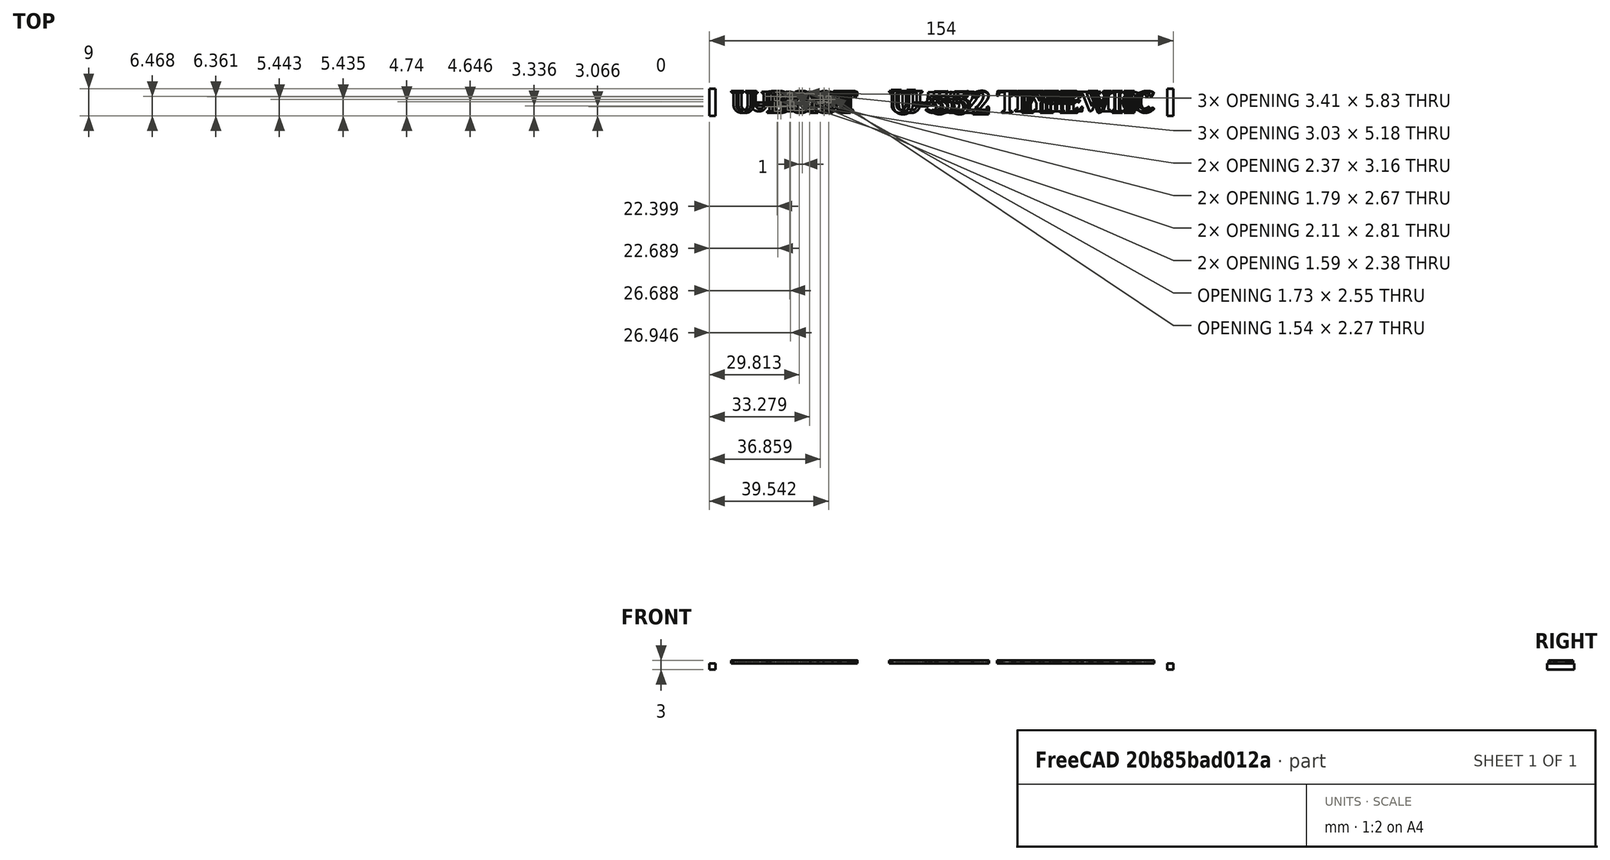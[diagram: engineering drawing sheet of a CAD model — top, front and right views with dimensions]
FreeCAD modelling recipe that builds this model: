
FCSTD DOCUMENT  (FreeCAD 0.18R16146 (Git))
Label: U-Boat Stand Nameplate
License: All rights reserved
LicenseURL: http://en.wikipedia.org/wiki/All_rights_reserved
objects: Part::FeaturePython×44, Part::Feature×12, Part::Part2DObjectPython×7, Part::Extrusion×7, App::DocumentObjectGroup×4, Sketcher::SketchObject×2, Part::Face×2, Part::Box×2, Mesh::Feature×1, Part::Compound×1
note: 77 computed .brp shape members not serialized (recipe doc carries the construction recipe); baked Part::Feature solids carry a one-line shape summary decoded from their .brp

FEATURE [Mesh::Feature] U_Boot_Stand_2  label="U-Boot-Stand-2"
FEATURE [Part::Feature] U_Boot_Stand_2001
  shape: bbox 154 x 20 x 3 mm, 3614 faces, 0 solids (baked)
FEATURE [Part::Feature] U_Boot_Stand_2001001  label="U_Boot_Stand_2002"
  shape: bbox 154 x 20 x 3 mm, 1660 faces, 0 solids (baked)
FEATURE [Sketcher::SketchObject] Sketch
  sketch-geometry (4):
    g0: LineSegment StartX=143.756 StartY=1.09319 StartZ=0 EndX=12.9474 EndY=1.09319 EndZ=0
    g1: LineSegment StartX=12.9474 StartY=1.09319 StartZ=0 EndX=12.9474 EndY=11.5235 EndZ=0
    g2: LineSegment StartX=12.9474 StartY=11.5235 StartZ=0 EndX=143.756 EndY=11.5235 EndZ=0
    g3: LineSegment StartX=143.756 StartY=11.5235 StartZ=0 EndX=143.756 EndY=1.09319 EndZ=0
  constraints (8):
    c: Coincident(g0,g1)
    c: Coincident(g1,g2)
    c: Coincident(g2,g3)
    c: Coincident(g3,g0)
    c: Horizontal(g0)
    c: Horizontal(g2)
    c: Vertical(g1)
    c: Vertical(g3)
FEATURE [Part::Face] Face
  FaceMakerClass = Part::FaceMakerBullseye
  Placement = pos=(0,1,2) rot=(0,0,1;0rad)
  Sources = -> [Sketch]
FEATURE [Part::FeaturePython] Slice  # WARN: FeaturePython — macro-defined, semantics opaque (R4)
  Base = -> U_Boot_Stand_2001001
  Mode = 1
  Tolerance = 0
  Tools = -> [Face]
FEATURE [Part::FeaturePython] Slice_child0  label="Slice.0"  # WARN: FeaturePython — macro-defined, semantics opaque (R4)
  Base = -> Slice
  FilterType = 1
  Invert = false
  OverrideMaxVal = 0
  WindowFrom = 80
  WindowTo = 100
  items = 0
FEATURE [Part::FeaturePython] Slice_child1  label="Slice.1"  # WARN: FeaturePython — macro-defined, semantics opaque (R4)
  Base = -> Slice
  FilterType = 1
  Invert = false
  OverrideMaxVal = 0
  WindowFrom = 80
  WindowTo = 100
  items = 1
FEATURE [Part::FeaturePython] Slice_child2  label="Slice.2"  # WARN: FeaturePython — macro-defined, semantics opaque (R4)
  Base = -> Slice
  FilterType = 1
  Invert = false
  OverrideMaxVal = 0
  WindowFrom = 80
  WindowTo = 100
  items = 2
FEATURE [Part::FeaturePython] Slice_child3  label="Slice.3"  # WARN: FeaturePython — macro-defined, semantics opaque (R4)
  Base = -> Slice
  FilterType = 1
  Invert = false
  OverrideMaxVal = 0
  WindowFrom = 80
  WindowTo = 100
  items = 3
FEATURE [Part::FeaturePython] Slice_child4  label="Slice.4"  # WARN: FeaturePython — macro-defined, semantics opaque (R4)
  Base = -> Slice
  FilterType = 1
  Invert = false
  OverrideMaxVal = 0
  WindowFrom = 80
  WindowTo = 100
  items = 4
FEATURE [Part::FeaturePython] Slice_child5  label="Slice.5"  # WARN: FeaturePython — macro-defined, semantics opaque (R4)
  Base = -> Slice
  FilterType = 1
  Invert = false
  OverrideMaxVal = 0
  WindowFrom = 80
  WindowTo = 100
  items = 5
FEATURE [Part::FeaturePython] Slice_child6  label="Slice.6"  # WARN: FeaturePython — macro-defined, semantics opaque (R4)
  Base = -> Slice
  FilterType = 1
  Invert = false
  OverrideMaxVal = 0
  WindowFrom = 80
  WindowTo = 100
  items = 6
FEATURE [Part::FeaturePython] Slice_child7  label="Slice.7"  # WARN: FeaturePython — macro-defined, semantics opaque (R4)
  Base = -> Slice
  FilterType = 1
  Invert = false
  OverrideMaxVal = 0
  WindowFrom = 80
  WindowTo = 100
  items = 7
FEATURE [Part::FeaturePython] Slice_child8  label="Slice.8"  # WARN: FeaturePython — macro-defined, semantics opaque (R4)
  Base = -> Slice
  FilterType = 1
  Invert = false
  OverrideMaxVal = 0
  WindowFrom = 80
  WindowTo = 100
  items = 8
FEATURE [Part::FeaturePython] Slice_child9  label="Slice.9"  # WARN: FeaturePython — macro-defined, semantics opaque (R4)
  Base = -> Slice
  FilterType = 1
  Invert = false
  OverrideMaxVal = 0
  WindowFrom = 80
  WindowTo = 100
  items = 9
FEATURE [Part::FeaturePython] Slice_child10  label="Slice.10"  # WARN: FeaturePython — macro-defined, semantics opaque (R4)
  Base = -> Slice
  FilterType = 1
  Invert = false
  OverrideMaxVal = 0
  WindowFrom = 80
  WindowTo = 100
  items = 10
FEATURE [Part::FeaturePython] Slice_child11  label="Slice.11"  # WARN: FeaturePython — macro-defined, semantics opaque (R4)
  Base = -> Slice
  FilterType = 1
  Invert = false
  OverrideMaxVal = 0
  WindowFrom = 80
  WindowTo = 100
  items = 11
FEATURE [Part::FeaturePython] Slice_child12  label="Slice.12"  # WARN: FeaturePython — macro-defined, semantics opaque (R4)
  Base = -> Slice
  FilterType = 1
  Invert = false
  OverrideMaxVal = 0
  WindowFrom = 80
  WindowTo = 100
  items = 12
FEATURE [Part::FeaturePython] Slice_child13  label="Slice.13"  # WARN: FeaturePython — macro-defined, semantics opaque (R4)
  Base = -> Slice
  FilterType = 1
  Invert = false
  OverrideMaxVal = 0
  WindowFrom = 80
  WindowTo = 100
  items = 13
FEATURE [Part::FeaturePython] Slice_child14  label="Slice.14"  # WARN: FeaturePython — macro-defined, semantics opaque (R4)
  Base = -> Slice
  FilterType = 1
  Invert = false
  OverrideMaxVal = 0
  WindowFrom = 80
  WindowTo = 100
  items = 14
FEATURE [Part::FeaturePython] Slice_child15  label="Slice.15"  # WARN: FeaturePython — macro-defined, semantics opaque (R4)
  Base = -> Slice
  FilterType = 1
  Invert = false
  OverrideMaxVal = 0
  WindowFrom = 80
  WindowTo = 100
  items = 15
FEATURE [Part::FeaturePython] Slice_child16  label="Slice.16"  # WARN: FeaturePython — macro-defined, semantics opaque (R4)
  Base = -> Slice
  FilterType = 1
  Invert = false
  OverrideMaxVal = 0
  WindowFrom = 80
  WindowTo = 100
  items = 16
FEATURE [Part::FeaturePython] Slice_child17  label="Slice.17"  # WARN: FeaturePython — macro-defined, semantics opaque (R4)
  Base = -> Slice
  FilterType = 1
  Invert = false
  OverrideMaxVal = 0
  WindowFrom = 80
  WindowTo = 100
  items = 17
FEATURE [Part::FeaturePython] Slice_child18  label="Slice.18"  # WARN: FeaturePython — macro-defined, semantics opaque (R4)
  Base = -> Slice
  FilterType = 1
  Invert = false
  OverrideMaxVal = 0
  WindowFrom = 80
  WindowTo = 100
  items = 18
FEATURE [Part::FeaturePython] Slice_child19  label="Slice.19"  # WARN: FeaturePython — macro-defined, semantics opaque (R4)
  Base = -> Slice
  FilterType = 1
  Invert = false
  OverrideMaxVal = 0
  WindowFrom = 80
  WindowTo = 100
  items = 19
FEATURE [Part::FeaturePython] Slice_child20  label="Slice.20"  # WARN: FeaturePython — macro-defined, semantics opaque (R4)
  Base = -> Slice
  FilterType = 1
  Invert = false
  OverrideMaxVal = 0
  WindowFrom = 80
  WindowTo = 100
  items = 20
FEATURE [Part::FeaturePython] Slice_child21  label="Slice.21"  # WARN: FeaturePython — macro-defined, semantics opaque (R4)
  Base = -> Slice
  FilterType = 1
  Invert = false
  OverrideMaxVal = 0
  WindowFrom = 80
  WindowTo = 100
  items = 21
FEATURE [Part::FeaturePython] Slice_child22  label="Slice.22"  # WARN: FeaturePython — macro-defined, semantics opaque (R4)
  Base = -> Slice
  FilterType = 1
  Invert = false
  OverrideMaxVal = 0
  WindowFrom = 80
  WindowTo = 100
  items = 22
FEATURE [Part::FeaturePython] Slice_child23  label="Slice.23"  # WARN: FeaturePython — macro-defined, semantics opaque (R4)
  Base = -> Slice
  FilterType = 1
  Invert = false
  OverrideMaxVal = 0
  WindowFrom = 80
  WindowTo = 100
  items = 23
FEATURE [Part::FeaturePython] Slice_child24  label="Slice.24"  # WARN: FeaturePython — macro-defined, semantics opaque (R4)
  Base = -> Slice
  FilterType = 1
  Invert = false
  OverrideMaxVal = 0
  WindowFrom = 80
  WindowTo = 100
  items = 24
FEATURE [Part::FeaturePython] Slice_child25  label="Slice.25"  # WARN: FeaturePython — macro-defined, semantics opaque (R4)
  Base = -> Slice
  FilterType = 1
  Invert = false
  OverrideMaxVal = 0
  WindowFrom = 80
  WindowTo = 100
  items = 25
FEATURE [App::DocumentObjectGroup] GrExplode_Slice  label="Exploded Slice"
  Group = -> [Slice_child0,Slice_child1,Slice_child2,Slice_child3,Slice_child4,Slice_child5,Slice_child6,Slice_child7,Slice_child8,Slice_child9,Slice_child10,Slice_child11,Slice_child12,Slice_child13,Slice_child14,Slice_child15,Slice_child16,Slice_child17,Slice_child18,Slice_child19,Slice_child20,Slice_child21,Slice_child22,Slice_child23,Slice_child24,Slice_child25]
FEATURE [Part::Feature] Slice_child9001  label="Slice.026"
  shape: bbox 154 x 20 x 2 mm, 48 faces, 0 solids (baked)
FEATURE [Part::Feature] Face001
  Placement = pos=(0,1,2) rot=(0,0,1;0rad)
  shape: bbox 130.8 x 10.43 x 2e-07 mm, 1 faces, 0 solids (baked)
FEATURE [Sketcher::SketchObject] Sketch001
  Placement = pos=(0,0,0) rot=(0.57735,0.57735,0.57735;2.0944rad)
  sketch-geometry (4):
    g0: LineSegment StartX=1.79046 StartY=2.35341 StartZ=0 EndX=12.2362 EndY=2.35341 EndZ=0
    g1: LineSegment StartX=12.2362 StartY=2.35341 StartZ=0 EndX=12.2362 EndY=-0.436562 EndZ=0
    g2: LineSegment StartX=12.2362 StartY=-0.436562 StartZ=0 EndX=1.79046 EndY=-0.436562 EndZ=0
    g3: LineSegment StartX=1.79046 StartY=-0.436562 StartZ=0 EndX=1.79046 EndY=2.35341 EndZ=0
  constraints (8):
    c: Coincident(g0,g1)
    c: Coincident(g1,g2)
    c: Coincident(g2,g3)
    c: Coincident(g3,g0)
    c: Horizontal(g0)
    c: Horizontal(g2)
    c: Vertical(g1)
    c: Vertical(g3)
FEATURE [Part::Face] Face002
  FaceMakerClass = Part::FaceMakerBullseye
  Placement = pos=(150,0,0) rot=(0,0,1;0rad)
  Sources = -> [Sketch001]
FEATURE [Part::FeaturePython] Slice001  # WARN: FeaturePython — macro-defined, semantics opaque (R4)
  Base = -> Face002
  Mode = 1
  Tolerance = 0
  Tools = -> [Slice_child9001]
FEATURE [Part::FeaturePython] Slice001_child0  label="Slice001.0"  # WARN: FeaturePython — macro-defined, semantics opaque (R4)
  Base = -> Slice001
  FilterType = 1
  Invert = false
  OverrideMaxVal = 0
  WindowFrom = 80
  WindowTo = 100
  items = 0
FEATURE [Part::FeaturePython] Slice001_child1  label="Slice001.1"  # WARN: FeaturePython — macro-defined, semantics opaque (R4)
  Base = -> Slice001
  FilterType = 1
  Invert = false
  OverrideMaxVal = 0
  WindowFrom = 80
  WindowTo = 100
  items = 1
FEATURE [Part::FeaturePython] Slice001_child2  label="Slice001.2"  # WARN: FeaturePython — macro-defined, semantics opaque (R4)
  Base = -> Slice001
  FilterType = 1
  Invert = false
  OverrideMaxVal = 0
  WindowFrom = 80
  WindowTo = 100
  items = 2
FEATURE [Part::FeaturePython] Slice001_child3  label="Slice001.3"  # WARN: FeaturePython — macro-defined, semantics opaque (R4)
  Base = -> Slice001
  FilterType = 1
  Invert = false
  OverrideMaxVal = 0
  WindowFrom = 80
  WindowTo = 100
  items = 3
FEATURE [Part::FeaturePython] Slice001_child4  label="Slice001.4"  # WARN: FeaturePython — macro-defined, semantics opaque (R4)
  Base = -> Slice001
  FilterType = 1
  Invert = false
  OverrideMaxVal = 0
  WindowFrom = 80
  WindowTo = 100
  items = 4
FEATURE [App::DocumentObjectGroup] GrExplode_Slice001  label="Exploded Slice001"
  Group = -> [Slice001_child0,Slice001_child1,Slice001_child2,Slice001_child3,Slice001_child4]
FEATURE [Part::Feature] Slice_child9001001  label="Slice.027"
  shape: bbox 154 x 20 x 2 mm, 48 faces, 0 solids (baked)
FEATURE [Part::Feature] Slice001_child4001  label="Slice001.005"
  shape: bbox 3e-07 x 10 x 2 mm, 1 faces, 0 solids (baked)
FEATURE [Part::Feature] Face002001  label="Face003"
  Placement = pos=(150,0,0) rot=(0,0,1;0rad)
  shape: bbox 2e-07 x 10.45 x 2.79 mm, 1 faces, 0 solids (baked)
FEATURE [Part::FeaturePython] Slice002  # WARN: FeaturePython — macro-defined, semantics opaque (R4)
  Base = -> Slice_child9001001
  Mode = 1
  Tolerance = 0
  Tools = -> [Face002001]
FEATURE [Part::FeaturePython] Slice002_child0  label="Slice002.0"  # WARN: FeaturePython — macro-defined, semantics opaque (R4)
  Base = -> Slice002
  FilterType = 1
  Invert = false
  OverrideMaxVal = 0
  WindowFrom = 80
  WindowTo = 100
  items = 0
FEATURE [Part::FeaturePython] Slice002_child1  label="Slice002.1"  # WARN: FeaturePython — macro-defined, semantics opaque (R4)
  Base = -> Slice002
  FilterType = 1
  Invert = false
  OverrideMaxVal = 0
  WindowFrom = 80
  WindowTo = 100
  items = 1
FEATURE [Part::FeaturePython] Slice002_child2  label="Slice002.2"  # WARN: FeaturePython — macro-defined, semantics opaque (R4)
  Base = -> Slice002
  FilterType = 1
  Invert = false
  OverrideMaxVal = 0
  WindowFrom = 80
  WindowTo = 100
  items = 2
FEATURE [Part::FeaturePython] Slice002_child3  label="Slice002.3"  # WARN: FeaturePython — macro-defined, semantics opaque (R4)
  Base = -> Slice002
  FilterType = 1
  Invert = false
  OverrideMaxVal = 0
  WindowFrom = 80
  WindowTo = 100
  items = 3
FEATURE [App::DocumentObjectGroup] GrExplode_Slice002  label="Exploded Slice002"
  Group = -> [Slice002_child0,Slice002_child1,Slice002_child2,Slice002_child3]
FEATURE [Part::Feature] Face002001001  label="Face004"
  shape: bbox 2e-07 x 10.45 x 2.79 mm, 1 faces, 0 solids (baked)
FEATURE [Part::FeaturePython] Slice003  # WARN: FeaturePython — macro-defined, semantics opaque (R4)
  Base = -> Slice002_child1
  Mode = 1
  Tolerance = 0
  Tools = -> [Face002001001]
FEATURE [Part::FeaturePython] Slice003_child0  label="Slice003.0"  # WARN: FeaturePython — macro-defined, semantics opaque (R4)
  Base = -> Slice003
  FilterType = 1
  Invert = false
  OverrideMaxVal = 0
  WindowFrom = 80
  WindowTo = 100
  items = 0
FEATURE [Part::FeaturePython] Slice003_child1  label="Slice003.1"  # WARN: FeaturePython — macro-defined, semantics opaque (R4)
  Base = -> Slice003
  FilterType = 1
  Invert = false
  OverrideMaxVal = 0
  WindowFrom = 80
  WindowTo = 100
  items = 1
FEATURE [Part::FeaturePython] Slice003_child2  label="Slice003.2"  # WARN: FeaturePython — macro-defined, semantics opaque (R4)
  Base = -> Slice003
  FilterType = 1
  Invert = false
  OverrideMaxVal = 0
  WindowFrom = 80
  WindowTo = 100
  items = 2
FEATURE [Part::FeaturePython] Slice003_child3  label="Slice003.3"  # WARN: FeaturePython — macro-defined, semantics opaque (R4)
  Base = -> Slice003
  FilterType = 1
  Invert = false
  OverrideMaxVal = 0
  WindowFrom = 80
  WindowTo = 100
  items = 3
FEATURE [App::DocumentObjectGroup] GrExplode_Slice003  label="Exploded Slice003"
  Group = -> [Slice003_child0,Slice003_child1,Slice003_child2,Slice003_child3]
FEATURE [Part::Feature] Slice001_child4002  label="Slice001.006"
  Placement = pos=(-150,0,0) rot=(0,0,1;0rad)
  shape: bbox 3e-07 x 10 x 2 mm, 1 faces, 0 solids (baked)
FEATURE [Part::Feature] Slice003_child2001  label="Slice003.004"
  shape: bbox 2e-07 x 0.2362 x 2 mm, 1 faces, 0 solids (baked)
FEATURE [Part::Feature] Slice003_child3001  label="Slice003.005"
  shape: bbox 2e-07 x 0.2095 x 2 mm, 1 faces, 0 solids (baked)
FEATURE [Part::FeaturePython] Connect  # WARN: FeaturePython — macro-defined, semantics opaque (R4)
  Objects = -> [Slice002_child2,Slice002_child3,Slice003_child1,Slice003_child2,Slice003_child2001,Face001,Slice003_child3001,Slice001_child4002,Slice003_child3,Slice001_child4001]
  Tolerance = 0
FEATURE [Part::Box] Box  label="Cube"
  AttacherType = Attacher::AttachEngine3D
  Height = 2
  Length = 2
  Placement = pos=(-2,2.5,0) rot=(0,0,1;0rad)
  Width = 9
FEATURE [Part::Box] Box001  label="Cube001"
  AttacherType = Attacher::AttachEngine3D
  Height = 2
  Length = 2
  Placement = pos=(150,2.5,0) rot=(0,0,1;0rad)
  Width = 9
FEATURE [Part::Compound] Compound
  Links = -> [Connect,Box,Box001]
FEATURE [Part::Feature] Compound001  label="Nameplate"
  shape: bbox 154 x 20 x 2.002 mm, 52 faces, 2 solids (baked)
FEATURE [Part::Part2DObjectPython] ShapeString  # Draft 2D object (typed FeaturePython)
  FontFile = <userpath>/.local/share/fonts/GenBkBasB.ttf
  Placement = pos=(6,3.5,3) rot=(0,0,1;0rad)
  Size = 9
  String = U-BOOT     U-552   TYP VIIC
  Tracking = 0
FEATURE [Part::Extrusion] Extrude  label="U-BOOT U-552 TYP VIIC"
  Base = -> ShapeString
  Dir = (0,0,1)
  DirMode = 2
  FaceMakerClass = Part::FaceMakerBullseye
  LengthFwd = 1
  LengthRev = 0
  Placement = pos=(0,0,-1) rot=(0,0,1;0rad)
  Solid = false
  Symmetric = false
FEATURE [Part::Part2DObjectPython] ShapeString001  # Draft 2D object (typed FeaturePython)
  FontFile = <userpath>/.local/share/fonts/GenBkBasB.ttf
  Placement = pos=(6,3.5,3) rot=(0,0,1;0rad)
  Size = 9
  String = U-BOAT    U-552  TYPE VIIC
  Tracking = 0
FEATURE [Part::Extrusion] Extrude001  label="U-BOAT U-552 TYPE VIIC"
  Base = -> ShapeString001
  Dir = (0,0,1)
  DirMode = 2
  FaceMakerClass = Part::FaceMakerBullseye
  LengthFwd = 1
  LengthRev = 0
  Placement = pos=(-1,0,-1) rot=(0,0,1;0rad)
  Solid = false
  Symmetric = false
FEATURE [Part::Part2DObjectPython] ShapeString002  label="T U-552"  # Draft 2D object (typed FeaturePython)
  FontFile = <userpath>/.local/share/fonts/GenBkBasB.ttf
  Size = 10
  String = U-552
  Tracking = 0
FEATURE [Part::Part2DObjectPython] ShapeString003  label="T U-BOOT"  # Draft 2D object (typed FeaturePython)
  FontFile = <userpath>/.local/share/fonts/GenBkBasB.ttf
  Size = 8
  String = U-BOOT
  Tracking = 0
FEATURE [Part::Part2DObjectPython] ShapeString004  label="T TYP VIIC"  # Draft 2D object (typed FeaturePython)
  FontFile = <userpath>/.local/share/fonts/GenBkBasB.ttf
  Size = 8
  String = TYP VIIC
  Tracking = 0
FEATURE [Part::Part2DObjectPython] ShapeString005  label="T U-BOAT"  # Draft 2D object (typed FeaturePython)
  FontFile = <userpath>/.local/share/fonts/GenBkBasB.ttf
  Size = 8
  String = U-BOAT
  Tracking = 0
FEATURE [Part::Part2DObjectPython] ShapeString006  label="T TYPE VIIC"  # Draft 2D object (typed FeaturePython)
  FontFile = <userpath>/.local/share/fonts/GenBkBasB.ttf
  Size = 8
  String = TYPE VIIC
  Tracking = 0
FEATURE [Part::Extrusion] Extrude002  label="U-552"
  Base = -> ShapeString002
  Dir = (0,0,1)
  DirMode = 2
  FaceMakerClass = Part::FaceMakerBullseye
  LengthFwd = 1
  LengthRev = 0
  Placement = pos=(58,3,2) rot=(0,0,1;0rad)
  Solid = false
  Symmetric = false
FEATURE [Part::Extrusion] Extrude005  label="U-Boat"
  Base = -> ShapeString005
  Dir = (0,0,1)
  DirMode = 2
  FaceMakerClass = Part::FaceMakerBullseye
  LengthFwd = 1
  LengthRev = 0
  Placement = pos=(11,4,2) rot=(0,0,1;0rad)
  Solid = false
  Symmetric = false
FEATURE [Part::Extrusion] Extrude006  label="TYPE VIIC"
  Base = -> ShapeString006
  Dir = (0,0,1)
  DirMode = 2
  FaceMakerClass = Part::FaceMakerBullseye
  LengthFwd = 1
  LengthRev = 0
  Placement = pos=(98,4,2) rot=(0,0,1;0rad)
  Solid = false
  Symmetric = false
FEATURE [Part::Extrusion] Extrude007  label="TYP VIIC"
  Base = -> ShapeString004
  Dir = (0,0,1)
  DirMode = 2
  FaceMakerClass = Part::FaceMakerBullseye
  LengthFwd = 1
  LengthRev = 0
  Placement = pos=(100,4,2) rot=(0,0,1;0rad)
  Solid = false
  Symmetric = false
FEATURE [Part::Extrusion] Extrude008  label="U-BOOT"
  Base = -> ShapeString003
  Dir = (0,0,1)
  DirMode = 2
  FaceMakerClass = Part::FaceMakerBullseye
  LengthFwd = 1
  LengthRev = 0
  Placement = pos=(11,4,2) rot=(0,0,1;0rad)
  Solid = false
  Symmetric = false
